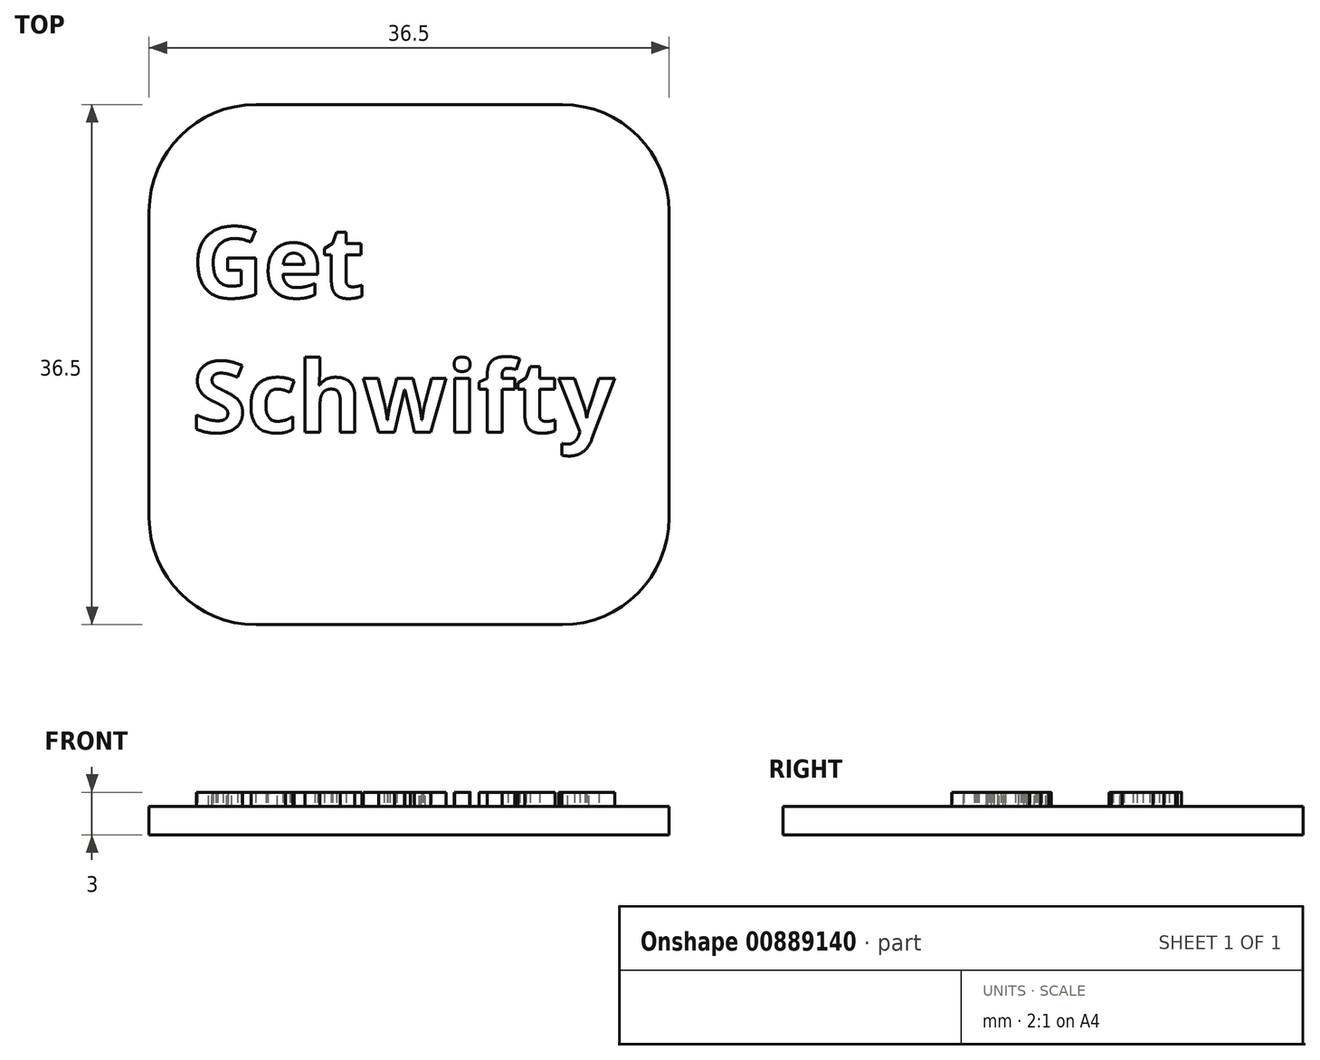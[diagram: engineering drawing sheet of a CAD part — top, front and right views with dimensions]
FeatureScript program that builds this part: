
annotation { "Feature Type Name" : "Feature", "Feature Type Description" : "" }
export const myFeature = defineFeature(function(context is Context, id is Id, definition is map)
    precondition{}
    {
        {
            var Q0;
            Q0=qCreatedBy(makeId("Top.planeOp"),FACE);
            var sketch = newSketch(context, id + "F0", { "sketchPlane" : qUnion([Q0])});
            skLineSegment(sketch, "E0.bottom", {"start": v(18.25, 18.25) * mm, "end": v(-18.25, 18.25) * mm});
            skLineSegment(sketch, "E0.top", {"start": v(18.25, -18.25) * mm, "end": v(-18.25, -18.25) * mm});
            skLineSegment(sketch, "E0.left", {"start": v(18.25, 18.25) * mm, "end": v(18.25, -18.25) * mm});
            skLineSegment(sketch, "E0.right", {"start": v(-18.25, 18.25) * mm, "end": v(-18.25, -18.25) * mm});
            skPoint(sketch, "E0.middle", {"position": v(0, 0) * mm});
            skSolve(sketch);
        }
        {
            var Q0;
            Q0 = qSketchRegion(id + "F0", true);
            extrude(context, id + "F1", {"entities" : qUnion([Q0]), "depth" : 2 * mm, "offsetDistance" : 25 * mm});
        }
        {
            var Q0;
            Q0=makeQuery(id+"F1.opExtrude","CAP_FACE",FACE,{"disambiguationData":[OSD([sQuery(id+"F0.wireOp",EDGE,"E0.bottom"),sQuery(id+"F0.wireOp",EDGE,"E0.top"),sQuery(id+"F0.wireOp",EDGE,"E0.left"),sQuery(id+"F0.wireOp",EDGE,"E0.right")])],"isStart":false});
            var sketch = newSketch(context, id + "F2", { "sketchPlane" : qUnion([Q0])});
            skText(sketch, "E1", { "text": "Get\nSchwifty", "fontName": "OpenSans-Bold.ttf"});
            const initialGuessF2  = {"E1": [-0.01524, 0.0047, 1, 0, 0.005]};
            skSetInitialGuess(sketch, initialGuessF2);
            skSolve(sketch);
        }
        {
            var Q0;
            Q0 = qSketchRegion(id + "F2", true);
            extrude(context, id + "F3", {"entities" : qUnion([Q0]), "operationType" : NewBodyOperationType.ADD, "depth" : 1 * mm, "offsetDistance" : 25 * mm});
        }
        {
            var Q0;
            Q0=makeQuery(id+"F1.opExtrude","SWEPT_EDGE",EDGE,{"disambiguationData":[OSD([sQuery(id+"F0.wireOp",EDGE,"E0.bottom"),sQuery(id+"F0.wireOp",EDGE,"E0.left")])]});
            var Q1;
            Q1=makeQuery(id+"F1.opExtrude","SWEPT_EDGE",EDGE,{"disambiguationData":[OSD([sQuery(id+"F0.wireOp",EDGE,"E0.bottom"),sQuery(id+"F0.wireOp",EDGE,"E0.right")])]});
            var Q2;
            Q2=makeQuery(id+"F1.opExtrude","SWEPT_EDGE",EDGE,{"disambiguationData":[OSD([sQuery(id+"F0.wireOp",EDGE,"E0.top"),sQuery(id+"F0.wireOp",EDGE,"E0.right")])]});
            var Q3;
            Q3=makeQuery(id+"F1.opExtrude","SWEPT_EDGE",EDGE,{"disambiguationData":[OSD([sQuery(id+"F0.wireOp",EDGE,"E0.top"),sQuery(id+"F0.wireOp",EDGE,"E0.left")])]});
            fillet(context, id + "F4", {"entities" : qUnion([Q0, Q1, Q2, Q3]), "radius" : 7.5 * mm, "tangentPropagation" : true, "allowEdgeOverflow" : false});
        }
    });
